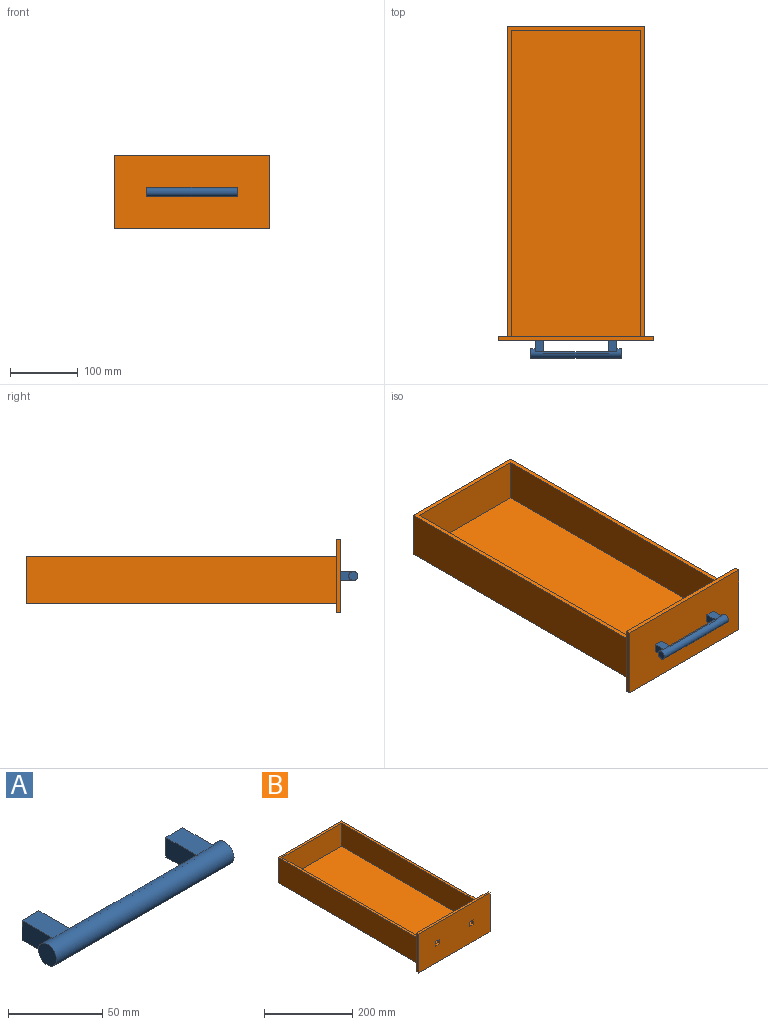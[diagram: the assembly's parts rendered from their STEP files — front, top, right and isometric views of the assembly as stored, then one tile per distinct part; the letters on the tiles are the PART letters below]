
ASSEMBLY  parts=2 mates=1
PART A: 16 faces, bbox 133.4x32.2x13.5 mm
  f0: plane 95.25x2.3mm, normal (0,0,-1), area 219.4mm2, adj f4,f7,f8,f12
  f1: plane 95.25x2.3mm, normal (0,0,1), area 219.4mm2, adj f4,f7,f8,f12
  f2: plane 23.1x12.7mm, normal (-1,0,0), area 252.2mm2, adj f3,f5,f6,f7
  f3: plane 23.1x12.7mm, normal (0,0,1), area 293.3mm2, adj f2,f4,f6,f7
  f4: plane 25.4x12.7mm, normal (1,0,0), area 322.6mm2, adj f0,f1,f3,f5,f6,f8
  f5: plane 23.1x12.7mm, normal (0,0,-1), area 293.3mm2, adj f2,f4,f6,f7
  f6: plane 12.7x12.7mm, normal (0,1,0), area 161.3mm2, adj f2,f3,f4,f5
  f7: cylinder r=6.75mm len=133.35mm, axis (-1,0,0), area 3666.5mm2, adj f0,f1,f2,f3,f5,f9,f10,f11
  f8: plane 95.25x12.7mm, normal (0,1,0), area 1209.7mm2, adj f0,f1,f4,f12
  f9: plane 13.51x13.51mm, normal (-1,0,0), area 143.3mm2, adj f7
  f10: plane 23.1x12.7mm, normal (1,0,0), area 252.2mm2, adj f7,f11,f13,f14
  f11: plane 23.1x12.7mm, normal (0,0,1), area 293.3mm2, adj f7,f10,f12,f14
  f12: plane 25.4x12.7mm, normal (-1,0,0), area 322.6mm2, adj f0,f1,f8,f11,f13,f14
  f13: plane 23.1x12.7mm, normal (0,0,-1), area 293.3mm2, adj f7,f10,f12,f14
  f14: plane 12.7x12.7mm, normal (0,1,0), area 161.3mm2, adj f10,f11,f12,f13
  f15: plane 13.51x13.51mm, normal (1,0,0), area 143.3mm2, adj f7
PART B: 23 faces, bbox 228.6x463.6x108 mm
  f0: plane 228.6x107.95mm, normal (0,1,0), area 22258mm2, adj f1,f2,f3,f4,f5,f6,f7,f8
  f1: plane 450.85x63.5mm, normal (1,0,0), area 28629mm2, adj f0,f10,f13,f14
  f2: plane 12.7x6.35mm, normal (-1,0,0), area 80.6mm2, adj f0,f3,f8,f9
  f3: plane 12.7x6.35mm, normal (0,0,1), area 80.6mm2, adj f0,f2,f4,f9
  f4: plane 12.7x6.35mm, normal (1,0,0), area 80.6mm2, adj f0,f3,f8,f9
  f5: plane 228.6x6.35mm, normal (0,0,-1), area 1451.6mm2, adj f0,f7,f9,f20
  f6: plane 228.6x6.35mm, normal (0,0,1), area 1451.6mm2, adj f0,f7,f9,f20
  f7: plane 107.95x6.35mm, normal (-1,0,0), area 685.5mm2, adj f0,f5,f6,f9
  f8: plane 12.7x6.35mm, normal (0,0,-1), area 80.6mm2, adj f0,f2,f4,f9
  f9: plane 228.6x107.95mm, normal (0,-1,0), area 24354.8mm2, adj f2,f3,f4,f5,f6,f7,f8,f17
  f10: plane 457.2x203.2mm, normal (0,0,1), area 7016.1mm2, adj f0,f1,f11,f12,f13,f16,f22
  f11: plane 457.2x69.85mm, normal (-1,0,0), area 31935.4mm2, adj f0,f10,f12,f15
  f12: plane 203.2x69.85mm, normal (0,1,0), area 14193.5mm2, adj f10,f11,f15,f22
  f13: plane 190.5x63.5mm, normal (0,-1,0), area 12096.8mm2, adj f1,f10,f14,f16
  f14: plane 450.85x190.5mm, normal (0,0,1), area 85886.9mm2, adj f0,f1,f13,f16
  f15: plane 457.2x203.2mm, normal (0,0,-1), area 92903mm2, adj f0,f11,f12,f22
  f16: plane 450.85x63.5mm, normal (-1,0,0), area 28629mm2, adj f0,f10,f13,f14
  f17: plane 12.7x6.35mm, normal (1,0,0), area 80.6mm2, adj f0,f9,f18,f21
  f18: plane 12.7x6.35mm, normal (0,0,1), area 80.6mm2, adj f0,f9,f17,f19
  f19: plane 12.7x6.35mm, normal (-1,0,0), area 80.6mm2, adj f0,f9,f18,f21
  f20: plane 107.95x6.35mm, normal (1,0,0), area 685.5mm2, adj f0,f5,f6,f9
  f21: plane 12.7x6.35mm, normal (0,0,-1), area 80.6mm2, adj f0,f9,f17,f19
  f22: plane 457.2x69.85mm, normal (1,0,0), area 31935.4mm2, adj f0,f10,f12,f15
PLACE A t=(0,0,6.51)mm
PLACE B at identity fixed
MATE fastened A.f6 <-> B.f0  axis (0,1,0) through (-60.33,0,0)mm
